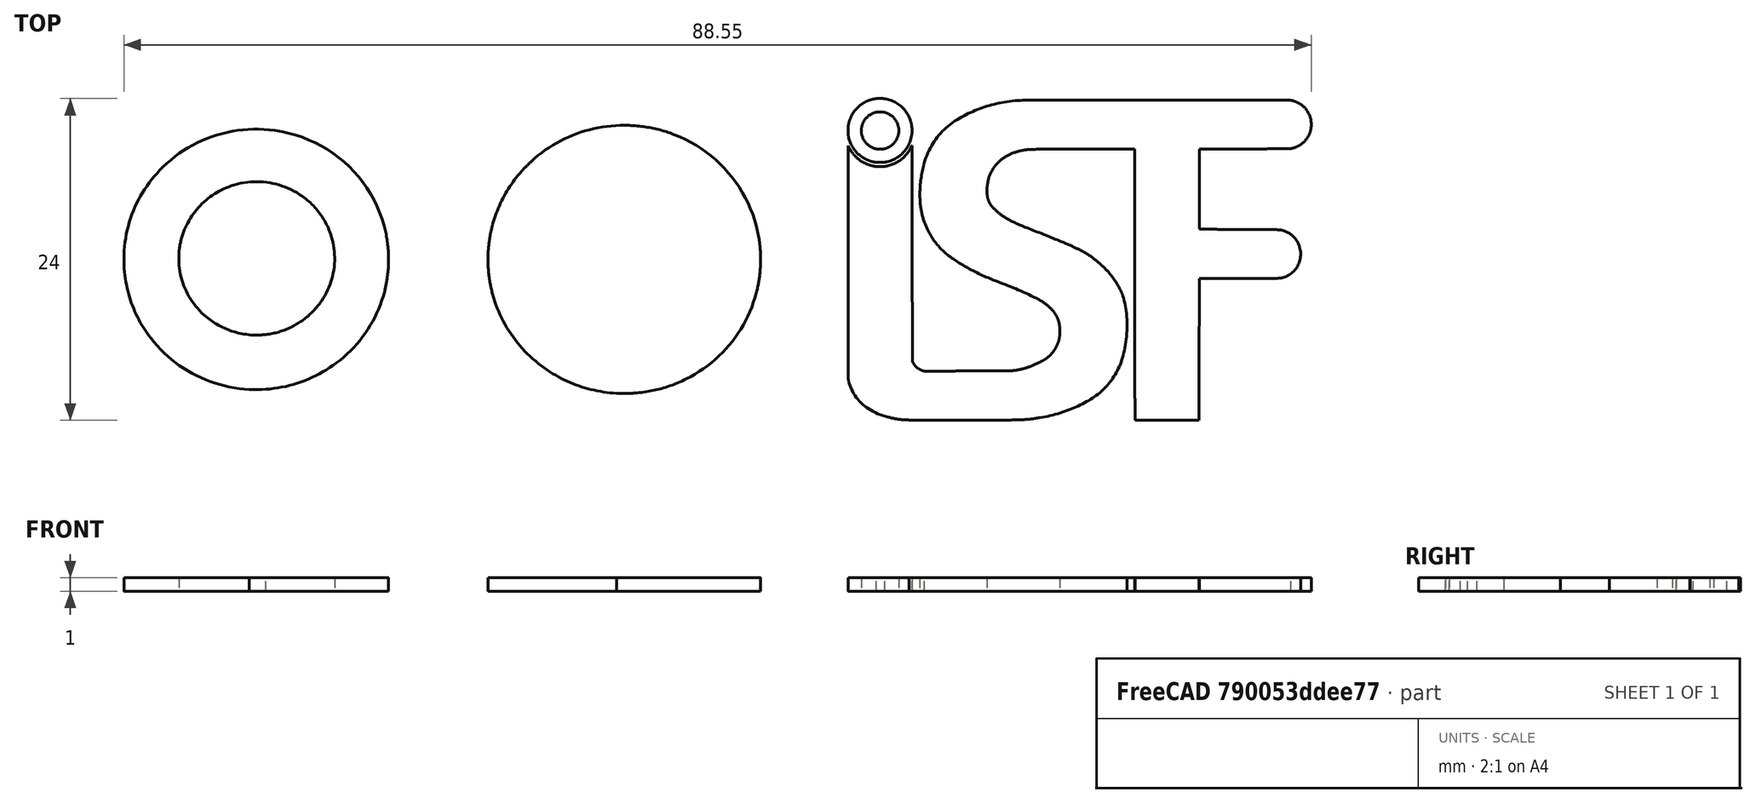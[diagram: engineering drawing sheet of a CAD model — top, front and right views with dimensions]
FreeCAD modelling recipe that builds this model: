
FCSTD DOCUMENT  (FreeCAD 0.21R33771 (Git))
Label: Logos
License: Creative Commons Attribution-ShareAlike 4.0
LicenseURL: https://creativecommons.org/licenses/by-sa/4.0/
objects: Part::Feature×6, Part::Extrusion×6, Part::Cut×2, Part::MultiFuse×2
note: 16 computed .brp shape members not serialized (recipe doc carries the construction recipe); baked Part::Feature solids carry a one-line shape summary decoded from their .brp

FEATURE [Part::Feature] path866
  shape: bbox 20.34 x 20.1 x 2e-07 mm, 1 faces, 0 solids (baked)
FEATURE [Part::Feature] path866001
  shape: bbox 19.8 x 19.86 x 2e-07 mm, 1 faces, 0 solids (baked)
FEATURE [Part::Feature] path866002
  shape: bbox 11.94 x 11.74 x 2e-07 mm, 1 faces, 0 solids (baked)
FEATURE [Part::Feature] path1325
  shape: bbox 34.57 x 23.9 x 2e-07 mm, 1 faces, 0 solids (baked)
FEATURE [Part::Feature] path1325001
  shape: bbox 4.801 x 4.781 x 2e-07 mm, 1 faces, 0 solids (baked)
FEATURE [Part::Feature] path1325002
  shape: bbox 2.844 x 2.781 x 2e-07 mm, 1 faces, 0 solids (baked)
FEATURE [Part::Extrusion] Extrude
  Base = -> path866
  Dir = (0,0,1)
  DirMode = 0
  FaceMakerClass = Part::FaceMakerBullseye
  LengthFwd = 1
  LengthRev = 0
  Solid = false
  Symmetric = false
FEATURE [Part::Extrusion] Extrude001
  Base = -> path866001
  Dir = (0,0,1)
  DirMode = 0
  FaceMakerClass = Part::FaceMakerBullseye
  LengthFwd = 1
  LengthRev = 0
  Solid = false
  Symmetric = false
FEATURE [Part::Extrusion] Extrude002
  Base = -> path866002
  Dir = (0,0,1)
  DirMode = 0
  FaceMakerClass = Part::FaceMakerBullseye
  LengthFwd = 1
  LengthRev = 0
  Solid = false
  Symmetric = false
FEATURE [Part::Extrusion] Extrude003
  Base = -> path1325
  Dir = (0,0,1)
  DirMode = 0
  FaceMakerClass = Part::FaceMakerBullseye
  LengthFwd = 1
  LengthRev = 0
  Solid = false
  Symmetric = false
FEATURE [Part::Extrusion] Extrude004
  Base = -> path1325001
  Dir = (0,0,1)
  DirMode = 0
  FaceMakerClass = Part::FaceMakerBullseye
  LengthFwd = 1
  LengthRev = 0
  Solid = false
  Symmetric = false
FEATURE [Part::Extrusion] Extrude005
  Base = -> path1325002
  Dir = (0,0,1)
  DirMode = 0
  FaceMakerClass = Part::FaceMakerBullseye
  LengthFwd = 1
  LengthRev = 0
  Solid = false
  Symmetric = false
FEATURE [Part::Cut] Cut
  Base = -> Extrude001
  Tool = -> Extrude002
FEATURE [Part::MultiFuse] Fusion  label="H-BRS"
  Shapes = -> [Extrude,Cut]
FEATURE [Part::Cut] Cut001
  Base = -> Extrude004
  Tool = -> Extrude005
FEATURE [Part::MultiFuse] Fusion001  label="ISF"
  Placement = pos=(54,2,0) rot=(0,0,1;0rad)
  Shapes = -> [Extrude003,Cut001]
